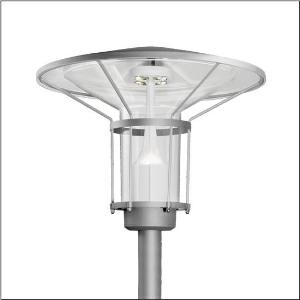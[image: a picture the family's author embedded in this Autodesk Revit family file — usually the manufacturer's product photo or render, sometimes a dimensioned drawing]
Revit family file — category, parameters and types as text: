
# Revit family: laterne_classic_iq___st1_2a_5xa5245kf14hp_f903
name_source: partatom
category: Lighting Fixtures
units: mm (PartAtom-declared; Revit-internal decimal feet)

## family parameters
Cut with Voids When Loaded = No
Host = Face
Light Source = No
Part Type = Normal
Room Calculation Point = No
Round Connector Dimension = Use Diameter
Shared = No

## types (1)
- --- (1 x LED, 4430 lm, 33.6 W, 4000K)
    Apparent Load = 34 VA
    CIE Flux Codes = 22 60 93 98 100
    Color Rendering = 70
    Color Temperature = 4000K
    Default Elevation = 1800 mm
    Description = Lantern Classic iQ, mast luminaire, Module 540 iQ-SR, primary light control with 3 zone facetted reflector, of plastic, silver coated, highly specular, structured, primary optical cover: cover, of PMMA, transparent, light distribution: ST1.2a, light emission: direct distribution, primary light characteristic: asymmetric, installation type: post-top, LED, High Power LED, rated luminous flux: 4.430lm, luminous efficacy: 132lm/W, light colour: 740, colour temperature: 4000K, control gear: ECG iQ, control: pre-setting: logarithmic dimming characteristic, Street-Remote, Auto-Match, Temp-Guard, Lumen-Switch, Night-Set, Smart-Wire, Light-Fading, Desk-Remote (wireless, voltage-free reading and setting of iQ features in the workshop via application-optimized NFC function/RFID function), optimised constant luminous flux control (CLO 2.0), with terminal, 6-pole, max. 2.5mm², mains connection: 230..240V, AC, 50/60Hz, start of lifetime: 34W, end of service life: 36W, reduction: 15W, luminaire housing, upper part, of glass-fibre reinforced polyester, coated, Siteco® metallic grey (DB 702S), diameter: 750mm, height: 596mm, spigot size: d x l = 76 x 70mm (post-top) | with reducer (optional accessory) 60 x 70mm, post-top mast mounting element, of diecast aluminium, coated, Siteco® metallic grey (DB 702S), Module 540 iQ-SR, traffic white (RAL 9016), equipment: Power, protection rating (complete): IP65, insulation class (complete): insulation class II (safety insulation), certification: CE, ENEC, VDE, packaging unit: 1 piece

Light Distribution: ST1.2a
    Height = 596 mm
    Lamp = 1 x LED
    Lamp Light Flux = 4430 lm
    Lamp Power = 33.6 W
    Lamp count = 1
    Length = 750 mm
    Luminous efficacy = 132 lm/W
    Manufacturer = Siteco
    ModVariant = No
    Model = 5XA5245KF14HP
    Number of Poles = 1
    OnlyDefault = Yes
    Power Factor = 1
    Product Name = Laterne Classic iQ | ST1.2a
    Product group = mast luminaire | pylon top
    ProductGroupID = 6100
    Protection Class = Protection class II
    Protection Degree = IP 65
    RLX_Detail_Level = 1
    RLX_Emergency_Light_Flux = 0 lm
    RLX_Emergency_Type = 0
    RLX_Emergency_Type_DB = No
    RlxData = <blob elided: 64953 chars, md5=f5b53168>
    Socket = socket
    Standby Power = 0 W
    System Light Flux = 4430 lm
    System Power = 34 W
    Type Comments = factory setting: luminous flux: 100 % | dim-lin: 254 | 695 mA
    Type Image = l_1006052.jpg
    URL = http://relux.com
    VarID = @adj_165925
    Voltage = 0 V
    Weight = 0.00 kg
    Width = 0 mm  [stored 0 ft]

note: [stored X ft] marks values corroborated as IEEE doubles in the binary element streams (Revit-internal decimal feet)

## geometry (parser evidence)
native form markers: Blend x4, Sweep x9
no freeform markers — native parametric forms only
